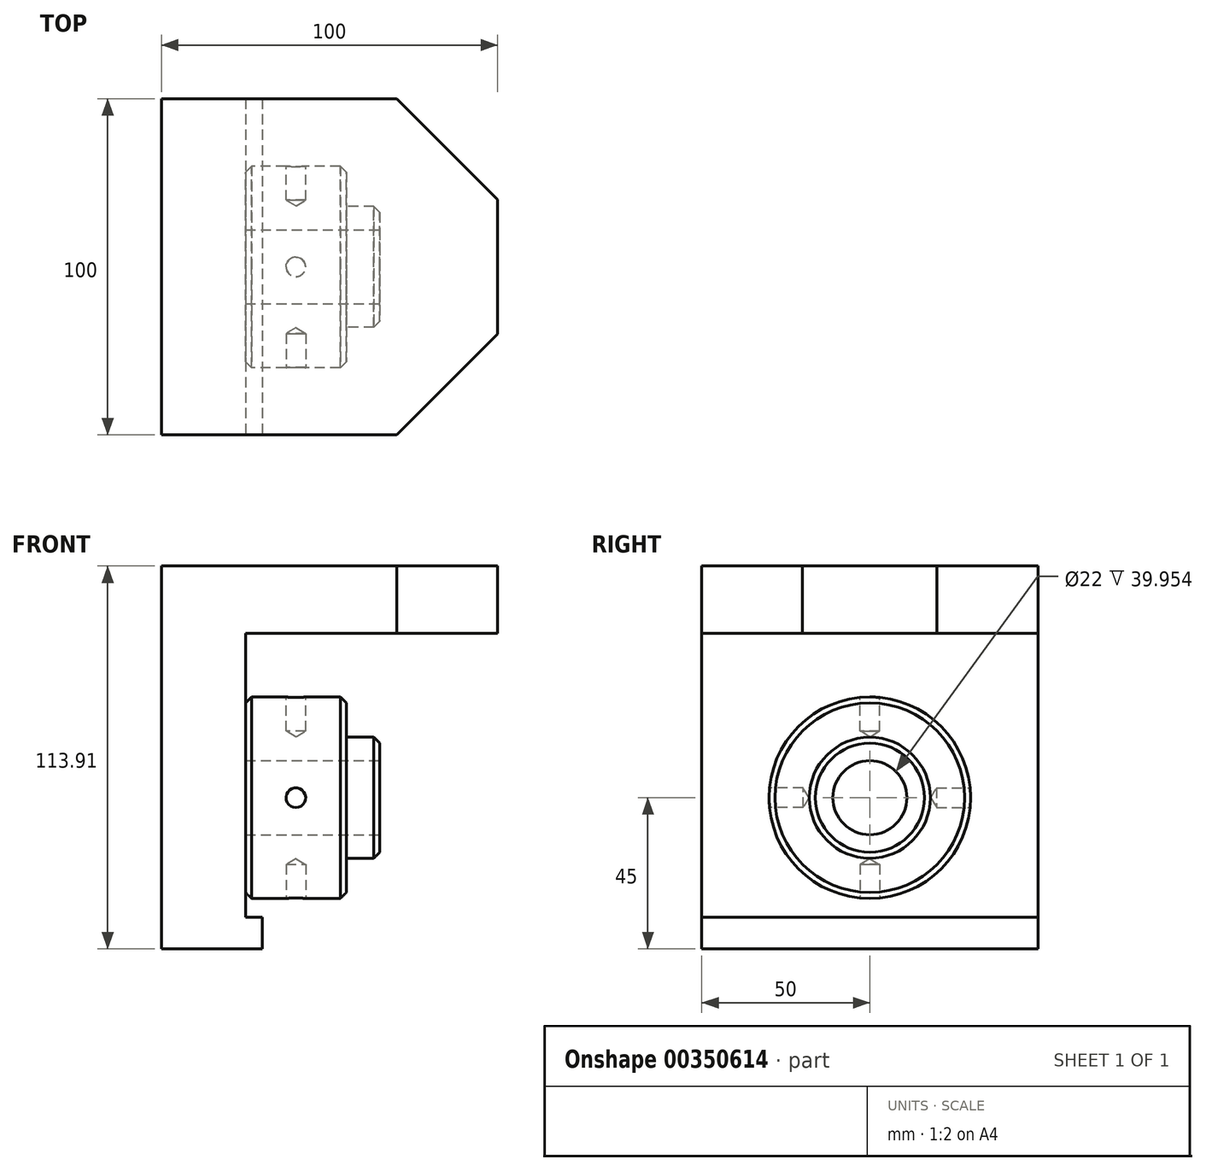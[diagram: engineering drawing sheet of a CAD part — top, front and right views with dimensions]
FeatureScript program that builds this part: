
annotation { "Feature Type Name" : "Feature", "Feature Type Description" : "" }
export const myFeature = defineFeature(function(context is Context, id is Id, definition is map)
    precondition{}
    {
        {
            var Q0;
            Q0=qCreatedBy(makeId("Right.planeOp"),FACE);
            var sketch = newSketch(context, id + "F0", { "sketchPlane" : qUnion([Q0])});
            skCircle(sketch, "E0", {"center": v(0, 0) * mm, "radius": 29.97 * mm});
            skSolve(sketch);
        }
        {
            var Q0;
            Q0=makeQuery(id+"F0.imprint","IMPRINT",FACE,{"disambiguationData":[TD([[makeQuery(id+"F0.imprint","IMPRINT",EDGE,{"derivedFrom":sQuery(id+"F0.wireOp",EDGE,"E0")}),1.0]])]});
            extrude(context, id + "F1", {"entities" : qUnion([Q0]), "depth" : 29.97 * mm});
        }
        {
            var Q0;
            Q0=makeQuery(id+"F1.opExtrude","CAP_FACE",FACE,{"disambiguationData":[OSD([sQuery(id+"F0.wireOp",EDGE,"E0")])],"isStart":false});
            var sketch = newSketch(context, id + "F2", { "sketchPlane" : qUnion([Q0])});
            skCircle(sketch, "E1", {"center": v(0, 0) * mm, "radius": 18 * mm});
            skSolve(sketch);
        }
        {
            var Q0;
            Q0=makeQuery(id+"F2.imprint","IMPRINT",FACE,{"disambiguationData":[TD([[makeQuery(id+"F2.imprint","IMPRINT",EDGE,{"derivedFrom":sQuery(id+"F2.wireOp",EDGE,"E1")}),1.0]])]});
            extrude(context, id + "F3", {"entities" : qUnion([Q0]), "operationType" : NewBodyOperationType.ADD, "depth" : 9.98 * mm});
        }
        {
            var Q0;
            Q0=makeQuery(id+"F3.opExtrude","CAP_FACE",FACE,{"disambiguationData":[OSD([sQuery(id+"F2.wireOp",EDGE,"E1")])],"isStart":false});
            var sketch = newSketch(context, id + "F4", { "sketchPlane" : qUnion([Q0])});
            skCircle(sketch, "E2", {"center": v(0, 0) * mm, "radius": 11 * mm});
            skSolve(sketch);
        }
        {
            var Q0;
            Q0=sQuery(id+"F4.wireOp",VERTEX,"E2.center");
            var Q1;
            Q1=makeQuery(id+"F1.opExtrude","SWEPT_BODY",BODY,{"disambiguationData":[OSD([sQuery(id+"F0.wireOp",EDGE,"E0")])]});
            hole(context, id + "F5", {"style" : HoleStyle.SIMPLE, "endStyle" : HoleEndStyle.THROUGH, "standardTappedOrClearance" : lookupTablePath({ "standard" : "사용자 정의" }), "standardBlindInLast" : lookupTablePath({ "standard" : "사용자 정의" }), "holeDiameter" : 22 * mm, "isTappedThrough" : true, "tappedDepth" : 12.7 * mm, "tapClearance" : 3, "locations" : qUnion([Q0]), "scope" : qUnion([Q1])});
        }
        {
            var Q0;
            Q0=makeQuery(id+"F1.opExtrude","CAP_EDGE",EDGE,{"disambiguationData":[OSD([sQuery(id+"F0.wireOp",EDGE,"E0")])],"isStart":true});
            chamfer(context, id + "F6", {"entities" : qUnion([Q0]), "width" : 1.78 * mm, "tangentPropagation" : true});
        }
        {
            var Q0;
            Q0=makeQuery(id+"F1.opExtrude","CAP_EDGE",EDGE,{"disambiguationData":[OSD([sQuery(id+"F0.wireOp",EDGE,"E0")])],"isStart":false});
            chamfer(context, id + "F7", {"entities" : qUnion([Q0]), "width" : 1.78 * mm, "tangentPropagation" : true});
        }
        {
            var Q0;
            Q0=qCreatedBy(makeId("Front.planeOp"),FACE);
            cPlane(context, id + "F8", {"entities" : qUnion([Q0]), "cplaneType" : CPlaneType.OFFSET, "offset" : 30 * mm, "width" : 152.4 * mm, "height" : 152.4 * mm});
        }
        {
            var Q0;
            Q0=qCreatedBy(makeId("Front.planeOp"),FACE);
            cPlane(context, id + "F9", {"entities" : qUnion([Q0]), "cplaneType" : CPlaneType.OFFSET, "offset" : 30 * mm, "oppositeDirection" : true, "width" : 152.4 * mm, "height" : 152.4 * mm});
        }
        {
            var Q0;
            Q0=qCreatedBy(makeId("Top.planeOp"),FACE);
            cPlane(context, id + "F10", {"entities" : qUnion([Q0]), "cplaneType" : CPlaneType.OFFSET, "offset" : 30 * mm, "width" : 152.4 * mm, "height" : 152.4 * mm});
        }
        {
            var Q0;
            Q0=qCreatedBy(makeId("Top.planeOp"),FACE);
            cPlane(context, id + "F11", {"entities" : qUnion([Q0]), "cplaneType" : CPlaneType.OFFSET, "offset" : 30 * mm, "oppositeDirection" : true, "width" : 152.4 * mm, "height" : 152.4 * mm});
        }
        {
            var Q0;
            Q0=qCreatedBy(id+"F8.planeOp",FACE);
            var sketch = newSketch(context, id + "F12", { "sketchPlane" : qUnion([Q0])});
            skPoint(sketch, "E3", {"position": v(14.99, 0) * mm});
            skSolve(sketch);
        }
        {
            var Q0;
            Q0=qCreatedBy(id+"F9.planeOp",FACE);
            var sketch = newSketch(context, id + "F13", { "sketchPlane" : qUnion([Q0])});
            skPoint(sketch, "E4", {"position": v(14.99, 0) * mm});
            skSolve(sketch);
        }
        {
            var Q0;
            Q0=sQuery(id+"F13.wireOp",VERTEX,"E4");
            var Q1;
            Q1=makeQuery(id+"F1.opExtrude","SWEPT_BODY",BODY,{"disambiguationData":[OSD([sQuery(id+"F0.wireOp",EDGE,"E0")])]});
            hole(context, id + "F14", {"style" : HoleStyle.SIMPLE, "endStyle" : HoleEndStyle.BLIND, "oppositeDirection" : true, "standardTappedOrClearance" : lookupTablePath({ "standard" : "사용자 정의" }), "standardBlindInLast" : lookupTablePath({ "standard" : "사용자 정의" }), "holeDiameter" : 5.84 * mm, "holeDepth" : 9.98 * mm, "isTappedThrough" : true, "tappedDepth" : 12.7 * mm, "tapClearance" : 3, "locations" : qUnion([Q0]), "scope" : qUnion([Q1])});
        }
        {
            var Q0;
            Q0=sQuery(id+"F12.wireOp",VERTEX,"E3");
            var Q1;
            Q1=makeQuery(id+"F1.opExtrude","SWEPT_BODY",BODY,{"disambiguationData":[OSD([sQuery(id+"F0.wireOp",EDGE,"E0")])]});
            hole(context, id + "F15", {"style" : HoleStyle.SIMPLE, "endStyle" : HoleEndStyle.BLIND, "standardTappedOrClearance" : lookupTablePath({ "standard" : "사용자 정의" }), "standardBlindInLast" : lookupTablePath({ "standard" : "사용자 정의" }), "holeDiameter" : 5.84 * mm, "holeDepth" : 9.98 * mm, "isTappedThrough" : true, "tappedDepth" : 12.7 * mm, "tapClearance" : 3, "locations" : qUnion([Q0]), "scope" : qUnion([Q1])});
        }
        {
            var Q0;
            Q0=qCreatedBy(id+"F10.planeOp",FACE);
            var sketch = newSketch(context, id + "F16", { "sketchPlane" : qUnion([Q0])});
            skPoint(sketch, "E5", {"position": v(14.99, 0) * mm});
            skSolve(sketch);
        }
        {
            var Q0;
            Q0=qCreatedBy(id+"F11.planeOp",FACE);
            var sketch = newSketch(context, id + "F17", { "sketchPlane" : qUnion([Q0])});
            skPoint(sketch, "E6", {"position": v(14.99, 0) * mm});
            skSolve(sketch);
        }
        {
            var Q0;
            Q0=sQuery(id+"F17.wireOp",VERTEX,"E6");
            var Q1;
            Q1=makeQuery(id+"F1.opExtrude","SWEPT_BODY",BODY,{"disambiguationData":[OSD([sQuery(id+"F0.wireOp",EDGE,"E0")])]});
            hole(context, id + "F18", {"style" : HoleStyle.SIMPLE, "endStyle" : HoleEndStyle.BLIND, "oppositeDirection" : true, "standardTappedOrClearance" : lookupTablePath({ "standard" : "사용자 정의" }), "standardBlindInLast" : lookupTablePath({ "standard" : "사용자 정의" }), "holeDiameter" : 5.84 * mm, "holeDepth" : 9.98 * mm, "isTappedThrough" : true, "tappedDepth" : 12.7 * mm, "tapClearance" : 3, "locations" : qUnion([Q0]), "scope" : qUnion([Q1])});
        }
        {
            var Q0;
            Q0=sQuery(id+"F16.wireOp",VERTEX,"E5");
            var Q1;
            Q1=makeQuery(id+"F1.opExtrude","SWEPT_BODY",BODY,{"disambiguationData":[OSD([sQuery(id+"F0.wireOp",EDGE,"E0")])]});
            hole(context, id + "F19", {"style" : HoleStyle.SIMPLE, "endStyle" : HoleEndStyle.BLIND, "standardTappedOrClearance" : lookupTablePath({ "standard" : "사용자 정의" }), "standardBlindInLast" : lookupTablePath({ "standard" : "사용자 정의" }), "holeDiameter" : 5.84 * mm, "holeDepth" : 9.98 * mm, "isTappedThrough" : true, "tappedDepth" : 12.7 * mm, "tapClearance" : 3, "locations" : qUnion([Q0]), "scope" : qUnion([Q1])});
        }
        {
            var Q0;
            Q0=makeQuery(id+"F3.opExtrude","CAP_EDGE",EDGE,{"disambiguationData":[OSD([sQuery(id+"F2.wireOp",EDGE,"E1")])],"isStart":false});
            chamfer(context, id + "F20", {"entities" : qUnion([Q0]), "width" : 1.78 * mm, "tangentPropagation" : true});
        }
        {
            var Q0;
            Q0=qCreatedBy(makeId("Front.planeOp"),FACE);
            var sketch = newSketch(context, id + "F21", { "sketchPlane" : qUnion([Q0])});
            skLineSegment(sketch, "E7", {"start": v(0, -45) * mm, "end": v(-25, -45) * mm});
            skLineSegment(sketch, "E8", {"start": v(-25, -45) * mm, "end": v(-25, 68.9) * mm});
            skLineSegment(sketch, "E9", {"start": v(-25, 68.9) * mm, "end": v(75, 68.9) * mm});
            skLineSegment(sketch, "E10", {"start": v(75, 68.9) * mm, "end": v(75, 48.9) * mm});
            skLineSegment(sketch, "E11", {"start": v(75, 48.9) * mm, "end": v(0, 48.9) * mm});
            skLineSegment(sketch, "E12", {"start": v(0, 48.9) * mm, "end": v(0, 0) * mm});
            skPoint(sketch, "E13.start.orphan", {"position": v(0, -82.24) * mm});
            skLineSegment(sketch, "E14", {"start": v(0, -45) * mm, "end": v(4.97, -45) * mm});
            skLineSegment(sketch, "E15", {"start": v(4.97, -45) * mm, "end": v(4.97, -35.6) * mm});
            skLineSegment(sketch, "E16", {"start": v(4.97, -35.6) * mm, "end": v(0, -35.6) * mm});
            skLineSegment(sketch, "E17", {"start": v(0, 0) * mm, "end": v(0, -35.6) * mm});
            skSolve(sketch);
        }
        {
            var Q0;
            Q0 = qSketchRegion(id + "F21", true);
            extrude(context, id + "F22", {"entities" : qUnion([Q0]), "operationType" : NewBodyOperationType.ADD, "endBound" : BoundingType.SYMMETRIC, "oppositeDirection" : true, "depth" : 100 * mm});
        }
        {
            var Q0;
            Q0=makeQuery(id+"F22.opExtrude","CAP_EDGE",EDGE,{"disambiguationData":[OSD([sQuery(id+"F21.wireOp",EDGE,"E10")])],"isStart":true});
            chamfer(context, id + "F23", {"entities" : qUnion([Q0]), "width" : 30 * mm, "tangentPropagation" : true});
        }
        {
            var Q0;
            Q0=makeQuery(id+"F22.opExtrude","CAP_EDGE",EDGE,{"disambiguationData":[OSD([sQuery(id+"F21.wireOp",EDGE,"E10")])],"isStart":false});
            chamfer(context, id + "F24", {"entities" : qUnion([Q0]), "width" : 30 * mm, "tangentPropagation" : true});
        }
    });
